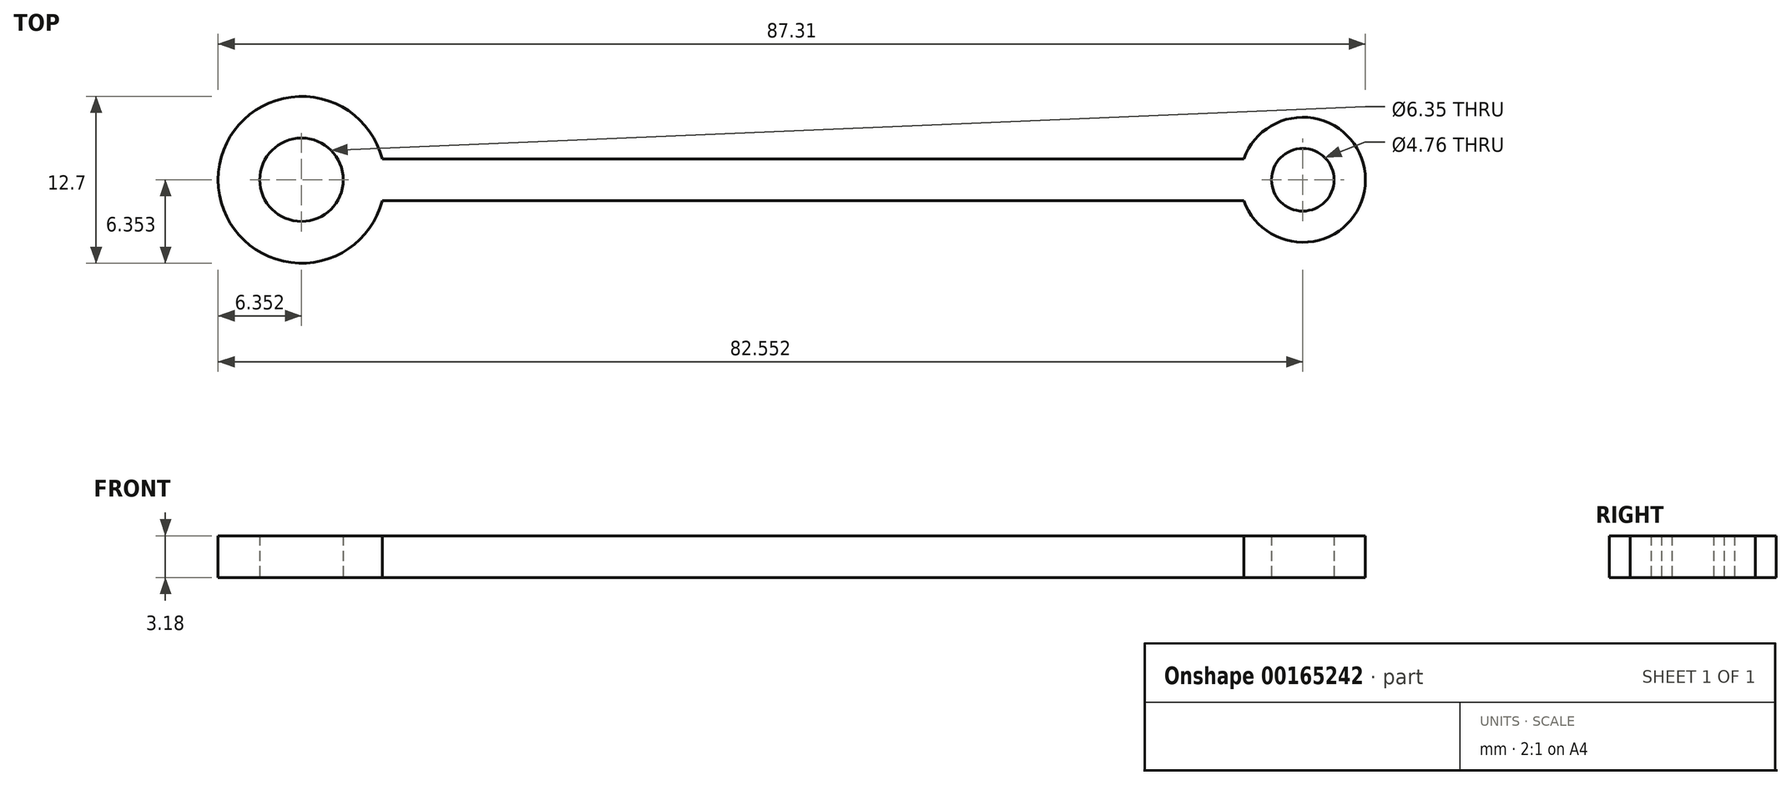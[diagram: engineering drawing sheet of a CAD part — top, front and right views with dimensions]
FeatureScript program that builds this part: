
annotation { "Feature Type Name" : "Feature", "Feature Type Description" : "" }
export const myFeature = defineFeature(function(context is Context, id is Id, definition is map)
    precondition{}
    {
        {
            var Q0;
            Q0=qCreatedBy(makeId("Top.planeOp"),FACE);
            var sketch = newSketch(context, id + "F0", { "sketchPlane" : qUnion([Q0])});
            skLineSegment(sketch, "E0.bottom", {"start": v(0, 0) * mm, "end": v(65.56, 0) * mm});
            skLineSegment(sketch, "E0.top", {"start": v(0, -3.18) * mm, "end": v(65.56, -3.18) * mm});
            skLineSegment(sketch, "E0.left", {"start": v(0, 0) * mm, "end": v(0, -3.18) * mm, "construction": true});
            skLineSegment(sketch, "E0.right", {"start": v(65.56, 0) * mm, "end": v(65.56, -3.17) * mm, "construction": true});
            skArc(sketch, "E1", {"start": v(0, 0) * mm, "mid": v(-12.5, -1.59) * mm, "end": v(0, -3.18) * mm});
            skArc(sketch, "E2", {"start": v(65.56, -3.18) * mm, "mid": v(74.81, -1.59) * mm, "end": v(65.56, 0) * mm});
            skLineSegment(sketch, "E3", {"start": v(-6.15, -1.59) * mm, "end": v(70.05, -1.59) * mm, "construction": true});
            skCircle(sketch, "E4", {"center": v(-6.15, -1.59) * mm, "radius": 3.18 * mm});
            skCircle(sketch, "E5", {"center": v(70.05, -1.59) * mm, "radius": 2.38 * mm});
            skSolve(sketch);
        }
        {
            var Q0;
            Q0 = qSketchRegion(id + "F0", true);
            extrude(context, id + "F1", {"entities" : qUnion([Q0]), "depth" : 3.17 * mm});
        }
    });
